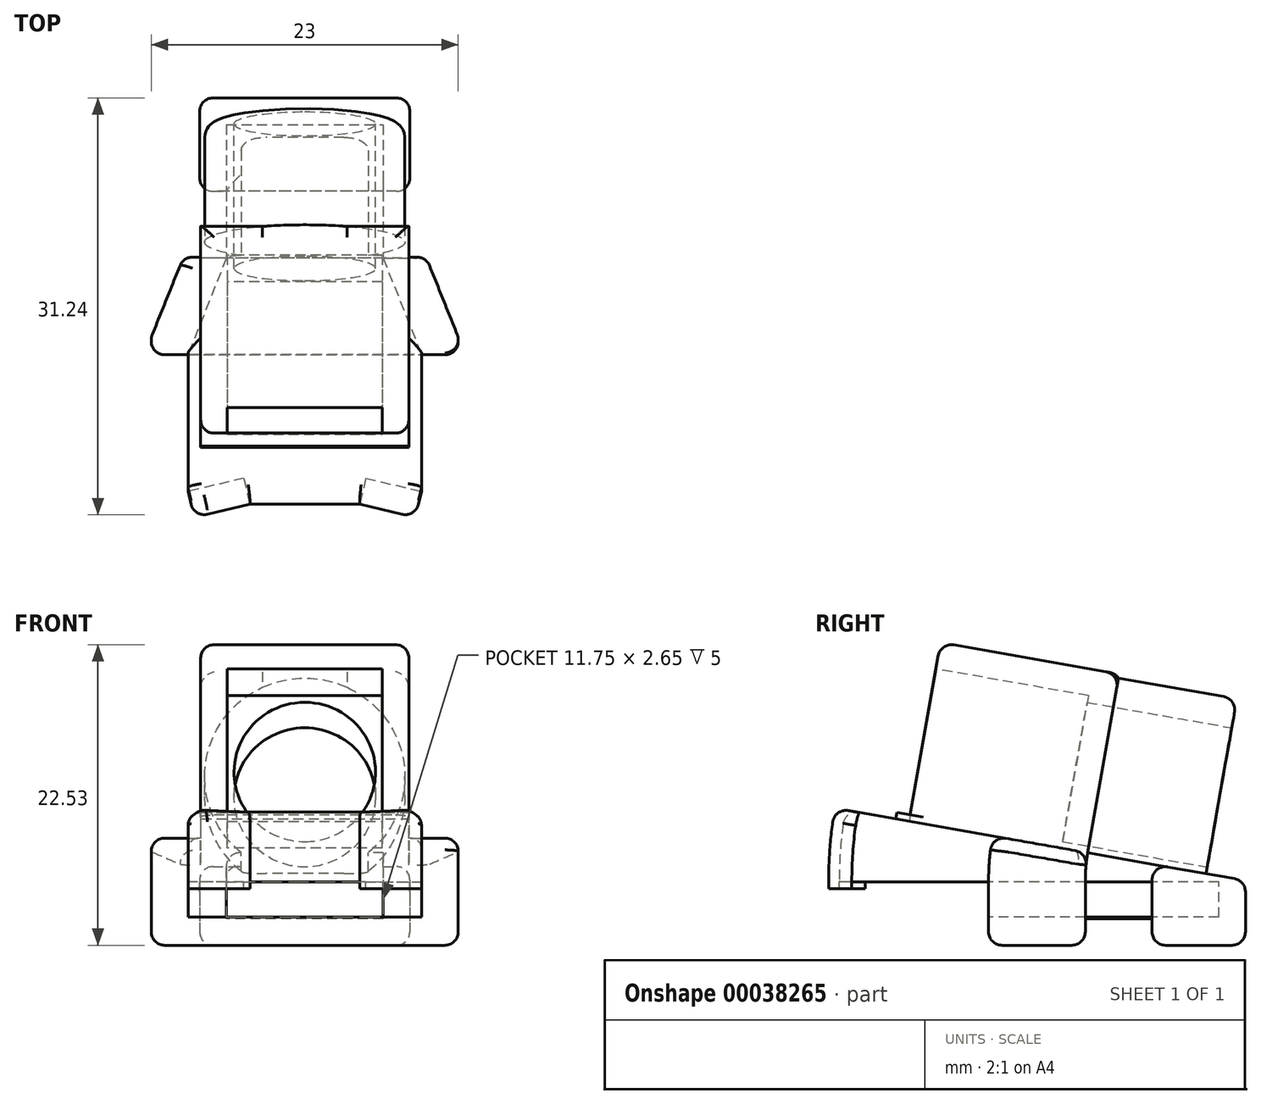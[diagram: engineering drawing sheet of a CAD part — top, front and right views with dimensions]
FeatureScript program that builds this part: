
annotation { "Feature Type Name" : "Feature", "Feature Type Description" : "" }
export const myFeature = defineFeature(function(context is Context, id is Id, definition is map)
    precondition{}
    {
        {
            var Q0;
            Q0=qCreatedBy(makeId("Top.planeOp"),FACE);
            var sketch = newSketch(context, id + "F0", { "sketchPlane" : qUnion([Q0])});
            skLineSegment(sketch, "E0", {"start": v(0, 0) * mm, "end": v(5.88, 0) * mm});
            skLineSegment(sketch, "E1", {"start": v(5.88, 0) * mm, "end": v(5.88, -10) * mm});
            skLineSegment(sketch, "E2.right", {"start": v(8.75, -17.25) * mm, "end": v(8.75, -26.5) * mm});
            skLineSegment(sketch, "E3", {"start": v(5.88, -10) * mm, "end": v(8.75, -17.25) * mm});
            skLineSegment(sketch, "E4", {"start": v(8.75, -26.5) * mm, "end": v(8.75, -27.5) * mm});
            skLineSegment(sketch, "E5", {"start": v(4.58, -26.5) * mm, "end": v(8.75, -27.5) * mm});
            skLineSegment(sketch, "E6.0", {"start": v(4.1, -28.44) * mm, "end": v(7.31, -29.21) * mm});
            skLineSegment(sketch, "E7", {"start": v(4.58, -26.5) * mm, "end": v(4.1, -28.44) * mm});
            skLineSegment(sketch, "E8", {"start": v(8.52, -28.47) * mm, "end": v(8.75, -27.5) * mm});
            skLineSegment(sketch, "E9.0", {"start": v(9.35, -10.63) * mm, "end": v(11.43, -15.88) * mm});
            skLineSegment(sketch, "E10", {"start": v(5.88, -10) * mm, "end": v(8.42, -10) * mm});
            skLineSegment(sketch, "E11", {"start": v(8.75, -17.25) * mm, "end": v(10.5, -17.25) * mm});
            skLineSegment(sketch, "E12.0", {"start": v(0, 2) * mm, "end": v(6.87, 2) * mm});
            skLineSegment(sketch, "E13.0", {"start": v(7.88, 1) * mm, "end": v(7.88, -4) * mm});
            skLineSegment(sketch, "E14", {"start": v(6.88, -5) * mm, "end": v(5.88, -5) * mm});
            skLineSegment(sketch, "E15.MirrorCS", {"start": v(-8.75, -26.5) * mm, "end": v(-8.75, -27.5) * mm});
            skLineSegment(sketch, "E16.MirrorCS", {"start": v(-8.52, -28.47) * mm, "end": v(-8.75, -27.5) * mm});
            skLineSegment(sketch, "E17.MirrorCS", {"start": v(0, 0) * mm, "end": v(-5.88, 0) * mm});
            skLineSegment(sketch, "E18.MirrorCS", {"start": v(-6.88, -5) * mm, "end": v(-5.87, -5) * mm});
            skLineSegment(sketch, "E19.MirrorCS", {"start": v(0, 2) * mm, "end": v(-6.88, 2) * mm});
            skLineSegment(sketch, "E20.MirrorCS", {"start": v(-5.88, 0) * mm, "end": v(-5.88, -10) * mm});
            skLineSegment(sketch, "E21.MirrorCS", {"start": v(-8.75, -17.25) * mm, "end": v(-10.5, -17.25) * mm});
            skLineSegment(sketch, "E22.MirrorCS", {"start": v(-5.88, -10) * mm, "end": v(-8.42, -10) * mm});
            skLineSegment(sketch, "E23.MirrorCS", {"start": v(-8.75, -17.25) * mm, "end": v(-8.75, -26.5) * mm});
            skLineSegment(sketch, "E24.MirrorCS", {"start": v(-5.88, -10) * mm, "end": v(-8.75, -17.25) * mm});
            skLineSegment(sketch, "E25.MirrorCS", {"start": v(-7.88, 1) * mm, "end": v(-7.88, -4) * mm});
            skLineSegment(sketch, "E26.MirrorCS", {"start": v(-4.58, -26.5) * mm, "end": v(-8.75, -27.5) * mm});
            skLineSegment(sketch, "E27.MirrorCS", {"start": v(-4.1, -28.44) * mm, "end": v(-7.31, -29.21) * mm});
            skLineSegment(sketch, "E28.MirrorCS", {"start": v(-9.35, -10.63) * mm, "end": v(-11.43, -15.88) * mm});
            skLineSegment(sketch, "E29.MirrorCS", {"start": v(-4.58, -26.5) * mm, "end": v(-4.1, -28.44) * mm});
            skLineSegment(sketch, "E30", {"start": v(-4.1, -28.44) * mm, "end": v(4.1, -28.44) * mm});
            skLineSegment(sketch, "E31", {"start": v(-8.75, -17.25) * mm, "end": v(8.75, -17.25) * mm});
            skPoint(sketch, "E32.visualSharp", {"position": v(-7.88, 2) * mm});
            skArc(sketch, "E32.filletArc", {"start": v(-6.88, 2) * mm, "mid": v(-7.58, 1.7) * mm, "end": v(-7.88, 1) * mm});
            skPoint(sketch, "E33.visualSharp", {"position": v(7.88, 2) * mm});
            skArc(sketch, "E33.filletArc", {"start": v(7.88, 1) * mm, "mid": v(7.58, 1.7) * mm, "end": v(6.87, 2) * mm});
            skPoint(sketch, "E34.visualSharp", {"position": v(-9.1, -10) * mm});
            skArc(sketch, "E34.filletArc", {"start": v(-8.42, -10) * mm, "mid": v(-8.98, -10.17) * mm, "end": v(-9.35, -10.63) * mm});
            skPoint(sketch, "E35.visualSharp", {"position": v(9.1, -10) * mm});
            skArc(sketch, "E35.filletArc", {"start": v(9.35, -10.63) * mm, "mid": v(8.98, -10.17) * mm, "end": v(8.42, -10) * mm});
            skPoint(sketch, "E36.visualSharp", {"position": v(-7.88, -5) * mm});
            skArc(sketch, "E36.filletArc", {"start": v(-7.88, -4) * mm, "mid": v(-7.58, -4.7) * mm, "end": v(-6.88, -5) * mm});
            skPoint(sketch, "E37.visualSharp", {"position": v(7.88, -5) * mm});
            skArc(sketch, "E37.filletArc", {"start": v(6.88, -5) * mm, "mid": v(7.58, -4.7) * mm, "end": v(7.88, -4) * mm});
            skPoint(sketch, "E38.visualSharp", {"position": v(-11.98, -17.25) * mm});
            skArc(sketch, "E38.filletArc", {"start": v(-11.43, -15.88) * mm, "mid": v(-11.33, -16.81) * mm, "end": v(-10.5, -17.25) * mm});
            skPoint(sketch, "E39.visualSharp", {"position": v(11.98, -17.25) * mm});
            skArc(sketch, "E39.filletArc", {"start": v(10.5, -17.25) * mm, "mid": v(11.33, -16.81) * mm, "end": v(11.43, -15.88) * mm});
            skPoint(sketch, "E40.visualSharp", {"position": v(-8.28, -29.44) * mm});
            skArc(sketch, "E40.filletArc", {"start": v(-8.52, -28.47) * mm, "mid": v(-8.07, -29.1) * mm, "end": v(-7.31, -29.21) * mm});
            skPoint(sketch, "E41.visualSharp", {"position": v(8.28, -29.44) * mm});
            skArc(sketch, "E41.filletArc", {"start": v(7.31, -29.21) * mm, "mid": v(8.07, -29.1) * mm, "end": v(8.52, -28.47) * mm});
            skSolve(sketch);
        }
        {
            var Q0;
            Q0 = qSketchRegion(id + "F0", true);
            extrude(context, id + "F1", {"entities" : qUnion([Q0]), "depth" : .1 * mm});
        }
        {
            var Q0;
            Q0=makeQuery(id+"F0.imprint","IMPRINT",FACE,{"disambiguationData":[TD([[makeQuery(id+"F0.imprint","IMPRINT",EDGE,{"derivedFrom":sQuery(id+"F0.wireOp",EDGE,"E16.MirrorCS")}),-1.0]])]});
            var Q1;
            Q1=makeQuery(id+"F0.imprint","IMPRINT",FACE,{"disambiguationData":[TD([[makeQuery(id+"F0.imprint","IMPRINT",EDGE,{"derivedFrom":sQuery(id+"F0.wireOp",EDGE,"E5")}),-1.0]])]});
            extrude(context, id + "F2", {"entities" : qUnion([Q0, Q1]), "operationType" : NewBodyOperationType.ADD, "oppositeDirection" : true, "depth" : .5 * mm});
        }
        {
            var Q0;
            Q0=makeQuery(id+"F0.imprint","IMPRINT",FACE,{"disambiguationData":[TD([[makeQuery(id+"F0.imprint","IMPRINT",EDGE,{"derivedFrom":sQuery(id+"F0.wireOp",EDGE,"E21.MirrorCS")}),-1.0]])]});
            var Q1;
            {var subQ6=sQuery(id+"F0.wireOp",EDGE,"E0");Q1=makeQuery(id+"F0.imprint","IMPRINT",FACE,{"disambiguationData":[TD([[makeQuery(id+"F0.imprint","IMPRINT",EDGE,{"derivedFrom":subQ6}),-1.0]])]});}
            var Q2;
            Q2=makeQuery(id+"F0.imprint","IMPRINT",FACE,{"disambiguationData":[TD([[makeQuery(id+"F0.imprint","IMPRINT",EDGE,{"derivedFrom":sQuery(id+"F0.wireOp",EDGE,"E3")}),1.0]])]});
            var Q3;
            {var subQ5=sQuery(id+"F0.wireOp",EDGE,"E0");Q3=makeQuery(id+"F0.imprint","IMPRINT",FACE,{"disambiguationData":[TD([[makeQuery(id+"F0.imprint","IMPRINT",EDGE,{"derivedFrom":subQ5}),1.0]])]});}
            extrude(context, id + "F3", {"entities" : qUnion([Q0, Q1, Q2, Q3]), "operationType" : NewBodyOperationType.ADD, "oppositeDirection" : true, "depth" : 2.75 * mm});
        }
        {
            var Q0;
            Q0=makeQuery(id+"F3.opExtrude","CAP_FACE",FACE,{"disambiguationData":[OSD([sQuery(id+"F0.wireOp",EDGE,"E1"),sQuery(id+"F0.wireOp",EDGE,"E9.0"),sQuery(id+"F0.wireOp",EDGE,"E10"),sQuery(id+"F0.wireOp",EDGE,"E11"),sQuery(id+"F0.wireOp",EDGE,"E12.0"),sQuery(id+"F0.wireOp",EDGE,"E13.0"),sQuery(id+"F0.wireOp",EDGE,"E14"),sQuery(id+"F0.wireOp",EDGE,"E18.MirrorCS"),sQuery(id+"F0.wireOp",EDGE,"E19.MirrorCS"),sQuery(id+"F0.wireOp",EDGE,"E20.MirrorCS"),sQuery(id+"F0.wireOp",EDGE,"E21.MirrorCS"),sQuery(id+"F0.wireOp",EDGE,"E22.MirrorCS"),sQuery(id+"F0.wireOp",EDGE,"E25.MirrorCS"),sQuery(id+"F0.wireOp",EDGE,"E28.MirrorCS"),sQuery(id+"F0.wireOp",EDGE,"E31")])],"isStart":false});
            var sketch = newSketch(context, id + "F4", { "sketchPlane" : qUnion([Q0])});
            skLineSegment(sketch, "E42", {"start": v(-5.88, 10) * mm, "end": v(5.88, 10) * mm});
            skLineSegment(sketch, "E43", {"start": v(5.88, 5) * mm, "end": v(-5.88, 5) * mm});
            skSolve(sketch);
        }
        {
            var Q0;
            Q0=makeQuery(id+"F4.imprint","IMPRINT",FACE,{"disambiguationData":[TD([[makeQuery(id+"F4.imprint","IMPRINT",EDGE,{"derivedFrom":sQuery(id+"F4.wireOp",EDGE,"E42")}),1.0]])]});
            var Q1;
            Q1=makeQuery(id+"F4.imprint","IMPRINT",FACE,{"disambiguationData":[TD([[makeQuery(id+"F4.imprint","IMPRINT",EDGE,{"derivedFrom":sQuery(id+"F4.wireOp",EDGE,"E43")}),1.0]])]});
            extrude(context, id + "F5", {"entities" : qUnion([Q0, Q1]), "operationType" : NewBodyOperationType.ADD, "depth" : 2 * mm});
        }
        {
            var Q0;
            {var subQ6=sQuery(id+"F0.wireOp",EDGE,"E0");Q0=makeQuery(id+"F0.imprint","IMPRINT",FACE,{"disambiguationData":[TD([[makeQuery(id+"F0.imprint","IMPRINT",EDGE,{"derivedFrom":subQ6}),-1.0]])]});}
            extrude(context, id + "F6", {"entities" : qUnion([Q0]), "operationType" : NewBodyOperationType.REMOVE, "oppositeDirection" : true, "depth" : 2.65 * mm});
        }
        {
            var Q0;
            Q0=makeQuery(id+"F5.opExtrude","CAP_EDGE",EDGE,{"disambiguationData":[OSD([sQuery(id+"F0.wireOp",EDGE,"E12.0"),sQuery(id+"F0.wireOp",EDGE,"E19.MirrorCS")])],"isStart":false});
            var Q1;
            Q1=makeQuery(id+"F5.opExtrude","CAP_EDGE",EDGE,{"disambiguationData":[OSD([sQuery(id+"F0.wireOp",EDGE,"E10"),sQuery(id+"F0.wireOp",EDGE,"E22.MirrorCS"),sQuery(id+"F4.wireOp",EDGE,"E42")])],"isStart":false});
            fillet(context, id + "F7", {"entities" : qUnion([Q0, Q1]), "radius" : 1 * mm, "tangentPropagation" : true, "allowEdgeOverflow" : false});
        }
        {
            var Q0;
            Q0=makeQuery(id+"F1.opExtrude","CAP_FACE",FACE,{"disambiguationData":[OSD([sQuery(id+"F0.wireOp",EDGE,"E1"),sQuery(id+"F0.wireOp",EDGE,"E2.right"),sQuery(id+"F0.wireOp",EDGE,"E4"),sQuery(id+"F0.wireOp",EDGE,"E6.0"),sQuery(id+"F0.wireOp",EDGE,"E8"),sQuery(id+"F0.wireOp",EDGE,"E9.0"),sQuery(id+"F0.wireOp",EDGE,"E10"),sQuery(id+"F0.wireOp",EDGE,"E11"),sQuery(id+"F0.wireOp",EDGE,"E12.0"),sQuery(id+"F0.wireOp",EDGE,"E13.0"),sQuery(id+"F0.wireOp",EDGE,"E14"),sQuery(id+"F0.wireOp",EDGE,"E15.MirrorCS"),sQuery(id+"F0.wireOp",EDGE,"E16.MirrorCS"),sQuery(id+"F0.wireOp",EDGE,"E18.MirrorCS"),sQuery(id+"F0.wireOp",EDGE,"E19.MirrorCS"),sQuery(id+"F0.wireOp",EDGE,"E20.MirrorCS"),sQuery(id+"F0.wireOp",EDGE,"E21.MirrorCS"),sQuery(id+"F0.wireOp",EDGE,"E22.MirrorCS"),sQuery(id+"F0.wireOp",EDGE,"E23.MirrorCS"),sQuery(id+"F0.wireOp",EDGE,"E25.MirrorCS"),sQuery(id+"F0.wireOp",EDGE,"E27.MirrorCS"),sQuery(id+"F0.wireOp",EDGE,"E28.MirrorCS"),sQuery(id+"F0.wireOp",EDGE,"E30"),sQuery(id+"F0.wireOp",EDGE,"E32.filletArc"),sQuery(id+"F0.wireOp",EDGE,"E33.filletArc"),sQuery(id+"F0.wireOp",EDGE,"E34.filletArc"),sQuery(id+"F0.wireOp",EDGE,"E35.filletArc"),sQuery(id+"F0.wireOp",EDGE,"E36.filletArc"),sQuery(id+"F0.wireOp",EDGE,"E37.filletArc"),sQuery(id+"F0.wireOp",EDGE,"E38.filletArc"),sQuery(id+"F0.wireOp",EDGE,"E39.filletArc"),sQuery(id+"F0.wireOp",EDGE,"E40.filletArc"),sQuery(id+"F0.wireOp",EDGE,"E41.filletArc")])],"isStart":false});
            var Q1;
            Q1=makeQuery(id+"F1.opExtrude","CAP_EDGE",EDGE,{"disambiguationData":[OSD([sQuery(id+"F0.wireOp",EDGE,"E12.0"),sQuery(id+"F0.wireOp",EDGE,"E19.MirrorCS")])],"isStart":false});
            revolve(context, id + "F8", {"operationType" : NewBodyOperationType.ADD, "entities" : qUnion([Q0]), "axis" : qUnion([Q1]), "revolveType" : RevolveType.ONE_DIRECTION, "oppositeDirection" : true, "angle" : 10 * degree});
        }
        {
            var Q0;
            Q0=makeQuery(id+"F8.opRevolve","CAP_FACE",FACE,{"disambiguationData":[OSD([sQuery(id+"F0.wireOp",EDGE,"E1"),sQuery(id+"F0.wireOp",EDGE,"E2.right"),sQuery(id+"F0.wireOp",EDGE,"E4"),sQuery(id+"F0.wireOp",EDGE,"E6.0"),sQuery(id+"F0.wireOp",EDGE,"E8"),sQuery(id+"F0.wireOp",EDGE,"E9.0"),sQuery(id+"F0.wireOp",EDGE,"E10"),sQuery(id+"F0.wireOp",EDGE,"E11"),sQuery(id+"F0.wireOp",EDGE,"E12.0"),sQuery(id+"F0.wireOp",EDGE,"E13.0"),sQuery(id+"F0.wireOp",EDGE,"E14"),sQuery(id+"F0.wireOp",EDGE,"E15.MirrorCS"),sQuery(id+"F0.wireOp",EDGE,"E16.MirrorCS"),sQuery(id+"F0.wireOp",EDGE,"E18.MirrorCS"),sQuery(id+"F0.wireOp",EDGE,"E19.MirrorCS"),sQuery(id+"F0.wireOp",EDGE,"E20.MirrorCS"),sQuery(id+"F0.wireOp",EDGE,"E21.MirrorCS"),sQuery(id+"F0.wireOp",EDGE,"E22.MirrorCS"),sQuery(id+"F0.wireOp",EDGE,"E23.MirrorCS"),sQuery(id+"F0.wireOp",EDGE,"E25.MirrorCS"),sQuery(id+"F0.wireOp",EDGE,"E27.MirrorCS"),sQuery(id+"F0.wireOp",EDGE,"E28.MirrorCS"),sQuery(id+"F0.wireOp",EDGE,"E30"),sQuery(id+"F0.wireOp",EDGE,"E32.filletArc"),sQuery(id+"F0.wireOp",EDGE,"E33.filletArc"),sQuery(id+"F0.wireOp",EDGE,"E34.filletArc"),sQuery(id+"F0.wireOp",EDGE,"E35.filletArc"),sQuery(id+"F0.wireOp",EDGE,"E36.filletArc"),sQuery(id+"F0.wireOp",EDGE,"E37.filletArc"),sQuery(id+"F0.wireOp",EDGE,"E38.filletArc"),sQuery(id+"F0.wireOp",EDGE,"E39.filletArc"),sQuery(id+"F0.wireOp",EDGE,"E40.filletArc"),sQuery(id+"F0.wireOp",EDGE,"E41.filletArc")])],"isStart":false});
            var sketch = newSketch(context, id + "F9", { "sketchPlane" : qUnion([Q0])});
            skLineSegment(sketch, "E44", {"start": v(0, 1.95) * mm, "end": v(0, -10.05) * mm});
            skLineSegment(sketch, "E45", {"start": v(0, -10.05) * mm, "end": v(0, -17.85) * mm});
            skLineSegment(sketch, "E46.rect.bottom", {"start": v(5.8, -12.05) * mm, "end": v(-5.8, -12.05) * mm});
            skLineSegment(sketch, "E46.rect.top", {"start": v(5.8, -23.65) * mm, "end": v(-5.8, -23.65) * mm});
            skLineSegment(sketch, "E46.rect.left", {"start": v(5.8, -12.05) * mm, "end": v(5.8, -23.65) * mm});
            skLineSegment(sketch, "E46.rect.right", {"start": v(-5.8, -12.05) * mm, "end": v(-5.8, -23.65) * mm});
            skPoint(sketch, "E46.rect.middle", {"position": v(0, -17.85) * mm});
            skLineSegment(sketch, "E47.0", {"start": v(-7.8, -10.05) * mm, "end": v(-7.8, -23.65) * mm});
            skLineSegment(sketch, "E47.1", {"start": v(7.8, -10.05) * mm, "end": v(-7.8, -10.05) * mm});
            skLineSegment(sketch, "E47.2", {"start": v(7.8, -10.05) * mm, "end": v(7.8, -23.65) * mm});
            skLineSegment(sketch, "E48", {"start": v(-7.8, -23.65) * mm, "end": v(-5.8, -23.65) * mm});
            skLineSegment(sketch, "E49", {"start": v(5.8, -23.65) * mm, "end": v(7.8, -23.65) * mm});
            skLineSegment(sketch, "E50.bottom", {"start": v(-7.8, -23.65) * mm, "end": v(7.8, -23.65) * mm});
            skLineSegment(sketch, "E50.top", {"start": v(-7.8, -24.65) * mm, "end": v(7.8, -24.65) * mm});
            skLineSegment(sketch, "E50.left", {"start": v(-7.8, -23.65) * mm, "end": v(-7.8, -24.65) * mm});
            skLineSegment(sketch, "E50.right", {"start": v(7.8, -23.65) * mm, "end": v(7.8, -24.65) * mm});
            skSolve(sketch);
        }
        {
            var Q0;
            {var subQ2=sQuery(id+"F9.wireOp",EDGE,"E46.rect.right");Q0=makeQuery(id+"F9.imprint","IMPRINT",FACE,{"disambiguationData":[TD([[makeQuery(id+"F9.imprint","IMPRINT",EDGE,{"derivedFrom":subQ2}),-1.0]])]});}
            var Q1;
            {var subQ7=sQuery(id+"F9.wireOp",EDGE,"E46.rect.left");Q1=makeQuery(id+"F9.imprint","IMPRINT",FACE,{"disambiguationData":[TD([[makeQuery(id+"F9.imprint","IMPRINT",EDGE,{"derivedFrom":subQ7}),1.0]])]});}
            extrude(context, id + "F10", {"entities" : qUnion([Q0, Q1]), "operationType" : NewBodyOperationType.ADD, "depth" : 11.6 * mm});
        }
        {
            var Q0;
            Q0=makeQuery(id+"F9.imprint","IMPRINT",FACE,{"disambiguationData":[TD([[makeQuery(id+"F9.imprint","IMPRINT",EDGE,{"derivedFrom":sQuery(id+"F9.wireOp",EDGE,"E50.top")}),1.0]])]});
            extrude(context, id + "F11", {"entities" : qUnion([Q0]), "operationType" : NewBodyOperationType.ADD, "depth" : .5 * mm});
        }
        {
            var Q0;
            Q0=makeQuery(id+"F10.opExtrude","CAP_FACE",FACE,{"disambiguationData":[OSD([sQuery(id+"F9.wireOp",EDGE,"E46.rect.bottom"),sQuery(id+"F9.wireOp",EDGE,"E46.rect.left"),sQuery(id+"F9.wireOp",EDGE,"E46.rect.right"),sQuery(id+"F9.wireOp",EDGE,"E47.0"),sQuery(id+"F9.wireOp",EDGE,"E47.1"),sQuery(id+"F9.wireOp",EDGE,"E47.2"),sQuery(id+"F9.wireOp",EDGE,"E50.bottom")])],"isStart":false});
            var sketch = newSketch(context, id + "F12", { "sketchPlane" : qUnion([Q0])});
            skLineSegment(sketch, "E51.bottom", {"start": v(-7.8, -10.05) * mm, "end": v(7.8, -10.05) * mm});
            skLineSegment(sketch, "E51.top", {"start": v(-7.8, -23.65) * mm, "end": v(7.8, -23.65) * mm});
            skLineSegment(sketch, "E51.left", {"start": v(-7.8, -10.05) * mm, "end": v(-7.8, -23.65) * mm});
            skLineSegment(sketch, "E51.right", {"start": v(7.8, -10.05) * mm, "end": v(7.8, -23.65) * mm});
            skSolve(sketch);
        }
        {
            var Q0;
            Q0=makeQuery(id+"F12.imprint","IMPRINT",FACE,{"disambiguationData":[TD([[makeQuery(id+"F12.imprint","IMPRINT",EDGE,{"derivedFrom":sQuery(id+"F12.wireOp",EDGE,"E51.bottom")}),1.0]])]});
            var Q1;
            Q1=makeQuery(id+"F12.imprint","IMPRINT",FACE,{"disambiguationData":[TD([[makeQuery(id+"F12.imprint","IMPRINT",EDGE,{"derivedFrom":makeQuery(id+"F10.opExtrude","CAP_EDGE",EDGE,{"disambiguationData":[OSD([sQuery(id+"F9.wireOp",EDGE,"E46.rect.bottom")])],"isStart":false})}),1.0]])]});
            extrude(context, id + "F13", {"entities" : qUnion([Q0, Q1]), "operationType" : NewBodyOperationType.ADD, "depth" : 2 * mm});
        }
        {
            var Q0;
            Q0=makeQuery(id+"F13.boolean.opBoolean","MERGE",FACE,{"derivedFrom":[makeQuery(id+"F10.opExtrude","SWEPT_FACE",FACE,{"disambiguationData":[OSD([sQuery(id+"F9.wireOp",EDGE,"E47.1")])]}),makeQuery(id+"F13.opExtrude","SWEPT_FACE",FACE,{"disambiguationData":[OSD([sQuery(id+"F12.wireOp",EDGE,"E51.bottom")])]})]});
            var sketch = newSketch(context, id + "F14", { "sketchPlane" : qUnion([Q0])});
            skLineSegment(sketch, "E52", {"start": v(0, 14.05) * mm, "end": v(0, 6.25) * mm});
            skPoint(sketch, "E52.endSnap0", {"position": v(0, 14.05) * mm});
            skCircle(sketch, "E53", {"center": v(0, 6.25) * mm, "radius": 5.3 * mm});
            skCircle(sketch, "E54", {"center": v(0, 6.25) * mm, "radius": 7.5 * mm});
            skSolve(sketch);
        }
        {
            var Q0;
            Q0=makeQuery(id+"F14.imprint","IMPRINT",FACE,{"disambiguationData":[TD([[makeQuery(id+"F14.imprint","IMPRINT",EDGE,{"derivedFrom":sQuery(id+"F14.wireOp",EDGE,"E53")}),1.0]])]});
            extrude(context, id + "F15", {"entities" : qUnion([Q0]), "operationType" : NewBodyOperationType.REMOVE, "endBound" : BoundingType.SYMMETRIC, "oppositeDirection" : true, "depth" : 9 * mm});
        }
        {
            var Q0;
            Q0=makeQuery(id+"F14.imprint","IMPRINT",FACE,{"disambiguationData":[TD([[makeQuery(id+"F14.imprint","IMPRINT",EDGE,{"derivedFrom":sQuery(id+"F14.wireOp",EDGE,"E53")}),-1.0]])]});
            extrude(context, id + "F16", {"entities" : qUnion([Q0]), "operationType" : NewBodyOperationType.ADD, "depth" : 9 * mm});
        }
        {
            var Q0;
            Q0=makeQuery(id+"F13.opExtrude","CAP_FACE",FACE,{"disambiguationData":[OSD([sQuery(id+"F12.wireOp",EDGE,"E51.bottom"),sQuery(id+"F12.wireOp",EDGE,"E51.top"),sQuery(id+"F12.wireOp",EDGE,"E51.left"),sQuery(id+"F12.wireOp",EDGE,"E51.right")])],"isStart":false});
            var Q1;
            Q1=makeQuery(id+"F16.opExtrude","CAP_EDGE",EDGE,{"disambiguationData":[OSD([sQuery(id+"F14.wireOp",EDGE,"E54")])],"isStart":false});
            var Q2;
            Q2=makeQuery(id+"F13.boolean.opBoolean","MERGE",EDGE,{"derivedFrom":[makeQuery(id+"F10.opExtrude","SWEPT_EDGE",EDGE,{"disambiguationData":[OSD([sQuery(id+"F9.wireOp",EDGE,"E47.2"),sQuery(id+"F9.wireOp",EDGE,"E50.bottom"),sQuery(id+"F9.wireOp",EDGE,"E50.right")])]}),makeQuery(id+"F13.opExtrude","SWEPT_EDGE",EDGE,{"disambiguationData":[OSD([sQuery(id+"F12.wireOp",EDGE,"E51.top"),sQuery(id+"F12.wireOp",EDGE,"E51.right")])]})]});
            var Q3;
            Q3=makeQuery(id+"F13.boolean.opBoolean","MERGE",EDGE,{"derivedFrom":[makeQuery(id+"F10.opExtrude","SWEPT_EDGE",EDGE,{"disambiguationData":[OSD([sQuery(id+"F9.wireOp",EDGE,"E47.0"),sQuery(id+"F9.wireOp",EDGE,"E50.bottom"),sQuery(id+"F9.wireOp",EDGE,"E50.left")])]}),makeQuery(id+"F13.opExtrude","SWEPT_EDGE",EDGE,{"disambiguationData":[OSD([sQuery(id+"F12.wireOp",EDGE,"E51.top"),sQuery(id+"F12.wireOp",EDGE,"E51.left")])]})]});
            fillet(context, id + "F17", {"entities" : qUnion([Q0, Q1, Q2, Q3]), "radius" : 1 * mm, "tangentPropagation" : true, "allowEdgeOverflow" : false});
        }
        {
            var Q0;
            Q0=makeQuery(id+"F8.opRevolve","CAP_EDGE",EDGE,{"disambiguationData":[OSD([sQuery(id+"F0.wireOp",EDGE,"E20.MirrorCS")])],"isStart":false});
            var Q1;
            Q1=makeQuery(id+"F8.opRevolve","CAP_EDGE",EDGE,{"disambiguationData":[OSD([sQuery(id+"F0.wireOp",EDGE,"E36.filletArc")])],"isStart":false});
            var Q2;
            Q2=makeQuery(id+"F8.opRevolve","CAP_EDGE",EDGE,{"disambiguationData":[OSD([sQuery(id+"F0.wireOp",EDGE,"E28.MirrorCS")])],"isStart":false});
            var Q3;
            Q3=makeQuery(id+"F8.opRevolve","CAP_EDGE",EDGE,{"disambiguationData":[OSD([sQuery(id+"F0.wireOp",EDGE,"E15.MirrorCS"),sQuery(id+"F0.wireOp",EDGE,"E23.MirrorCS")])],"isStart":false});
            var Q4;
            Q4=makeQuery(id+"F8.opRevolve","CAP_EDGE",EDGE,{"disambiguationData":[OSD([sQuery(id+"F0.wireOp",EDGE,"E27.MirrorCS")])],"isStart":false});
            var Q5;
            Q5=makeQuery(id+"F8.opRevolve","CAP_EDGE",EDGE,{"disambiguationData":[OSD([sQuery(id+"F0.wireOp",EDGE,"E30")])],"isStart":false});
            var Q6;
            Q6=makeQuery(id+"F8.opRevolve","CAP_EDGE",EDGE,{"disambiguationData":[OSD([sQuery(id+"F0.wireOp",EDGE,"E6.0")])],"isStart":false});
            var Q7;
            Q7=makeQuery(id+"F8.opRevolve","CAP_EDGE",EDGE,{"disambiguationData":[OSD([sQuery(id+"F0.wireOp",EDGE,"E2.right"),sQuery(id+"F0.wireOp",EDGE,"E4")])],"isStart":false});
            var Q8;
            Q8=makeQuery(id+"F8.opRevolve","CAP_EDGE",EDGE,{"disambiguationData":[OSD([sQuery(id+"F0.wireOp",EDGE,"E9.0")])],"isStart":false});
            fillet(context, id + "F18", {"entities" : qUnion([Q0, Q1, Q2, Q3, Q4, Q5, Q6, Q7, Q8]), "radius" : 1 * mm, "tangentPropagation" : true, "allowEdgeOverflow" : false});
        }
    });
